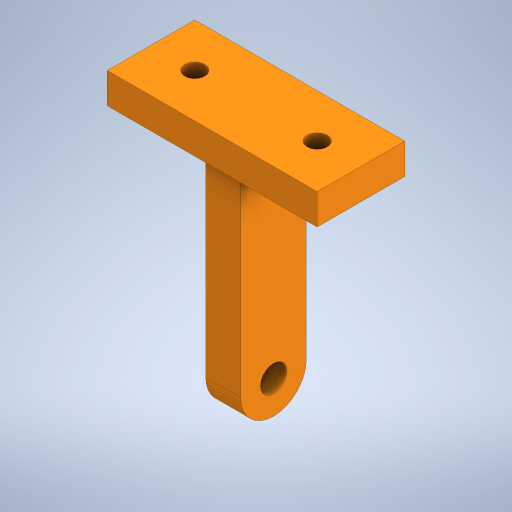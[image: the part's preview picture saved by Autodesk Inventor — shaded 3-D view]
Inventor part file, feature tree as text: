
AUTODESK INVENTOR PART (.ipt)
format: ipt  version: 2023 (Build 270158000, 158)  size: 256,000 bytes
history: native  units: in
note: dims shown in document units (in); Inventor stores cm internally (conversion verified against a paired STEP export)
features: extrude x3, sketch x3
ambient origin geometry x8: Origin, YZ Plane, XZ Plane, XY Plane, X Axis, Y Axis, Z Axis, Center Point
bodies: Solid1 (feature_tree)
feature tree (6):
  extrude  "Extrusion1"  Depth=0.5906in
  extrude  "Extrusion2"  Depth=0.315in TaperAngle=0.0deg
  extrude  "Extrusion3"  Depth=0.0984in
  sketch  "Sketch1"  dims[d0=0.2362in d1=0.5906in]
  sketch  "Sketch2"  dims[d2=1.7717in d3=0.315in d4=0.0in]
  sketch  "Sketch3"  dims[d5=0.7874in d6=0.0984in d7=0.0in d8=0.2756in d9=0.7874in d10=1.1024in d11=0.0in d12=0.0in d13=0.3937in d14=0.3937in d15=0.1811in d16=0.1811in d17=0.3937in d18=0.3937in d19=0.7874in d20=0.0in]
